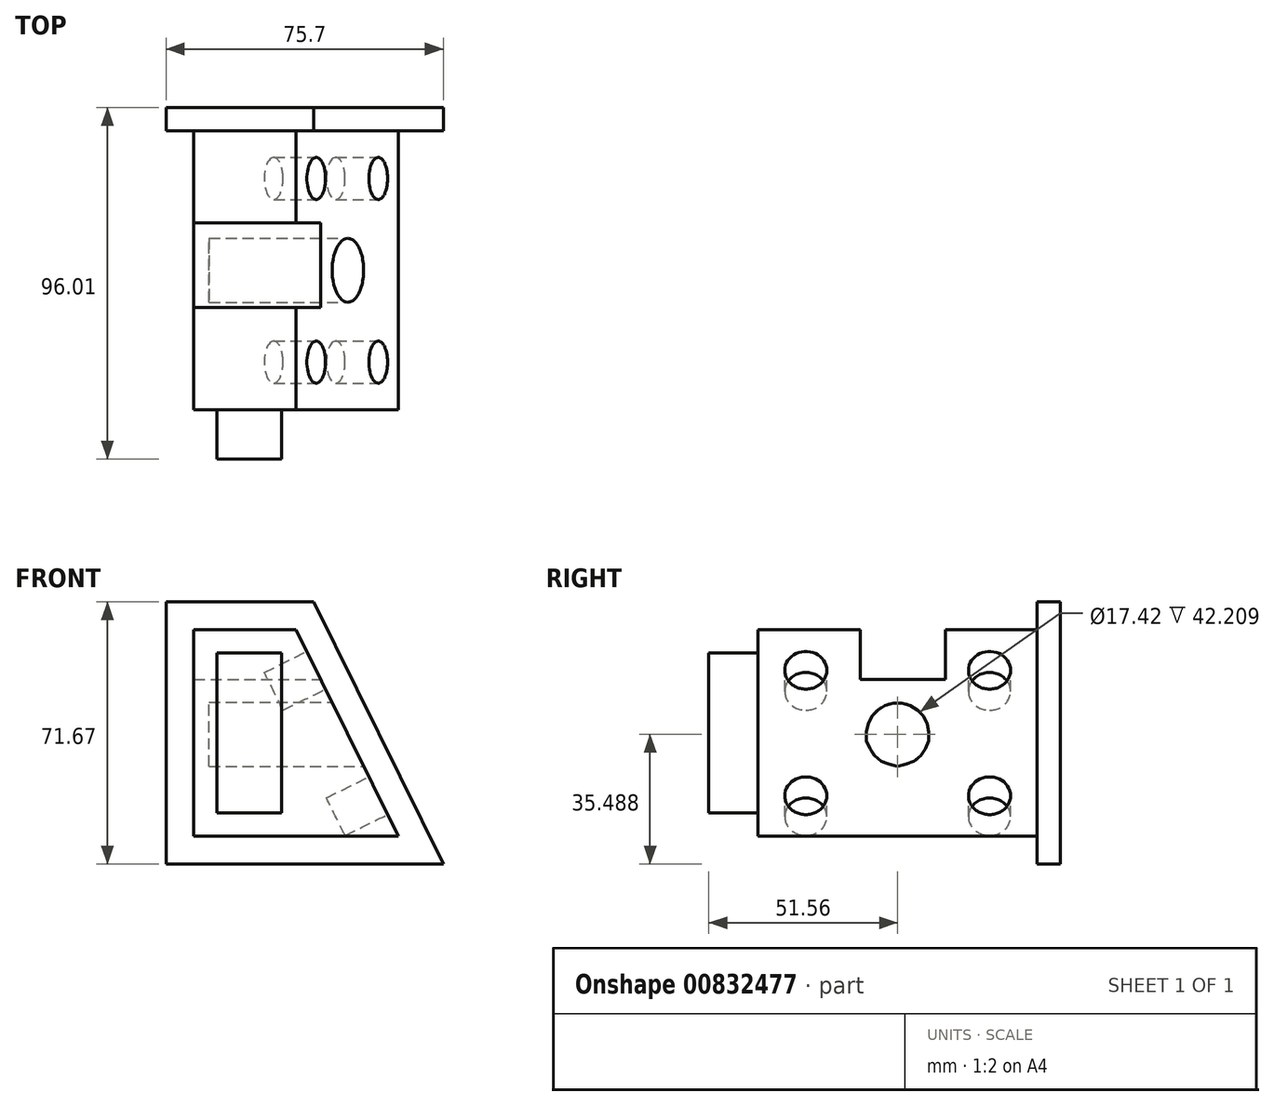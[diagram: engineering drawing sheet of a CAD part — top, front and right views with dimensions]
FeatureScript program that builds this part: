
annotation { "Feature Type Name" : "Feature", "Feature Type Description" : "" }
export const myFeature = defineFeature(function(context is Context, id is Id, definition is map)
    precondition{}
    {
        {
            var Q0;
            Q0=qCreatedBy(makeId("Front.planeOp"),FACE);
            var sketch = newSketch(context, id + "F0", { "sketchPlane" : qUnion([Q0])});
            skLineSegment(sketch, "E0.bottom", {"start": v(29.58, 0) * mm, "end": v(-26.23, 0) * mm});
            skLineSegment(sketch, "E0.right", {"start": v(-26.23, 0) * mm, "end": v(-26.23, 56.43) * mm});
            skLineSegment(sketch, "E1", {"start": v(-26.23, 56.43) * mm, "end": v(1.68, 56.43) * mm});
            skLineSegment(sketch, "E2", {"start": v(1.68, 56.43) * mm, "end": v(29.58, 0) * mm});
            skPoint(sketch, "E3.orphan", {"position": v(29.58, 56.43) * mm});
            skSolve(sketch);
        }
        {
            var Q0;
            Q0 = qSketchRegion(id + "F0", true);
            extrude(context, id + "F1", {"entities" : qUnion([Q0]), "endBound" : BoundingType.SYMMETRIC, "depth" : 76.2 * mm, "offsetDistance" : 25.4 * mm});
        }
        {
            var Q0;
            Q0=qCreatedBy(makeId("Right.planeOp"),FACE);
            var sketch = newSketch(context, id + "F2", { "sketchPlane" : qUnion([Q0])});
            skCircle(sketch, "E4", {"center": v(0, 27.87) * mm, "radius": 8.7 * mm});
            skSolve(sketch);
        }
        {
            var Q0;
            Q0 = qSketchRegion(id + "F2", true);
            extrude(context, id + "F3", {"entities" : qUnion([Q0]), "operationType" : NewBodyOperationType.REMOVE, "endBound" : BoundingType.SYMMETRIC, "oppositeDirection" : true, "depth" : 44.2 * mm, "offsetDistance" : 25.4 * mm});
        }
        {
            var Q0;
            Q0=makeQuery(id+"F1.opExtrude","CAP_FACE",FACE,{"disambiguationData":[OSD([sQuery(id+"F0.wireOp",EDGE,"E0.bottom"),sQuery(id+"F0.wireOp",EDGE,"E0.right"),sQuery(id+"F0.wireOp",EDGE,"E1"),sQuery(id+"F0.wireOp",EDGE,"E2")])],"isStart":true});
            var sketch = newSketch(context, id + "F4", { "sketchPlane" : qUnion([Q0])});
            skLineSegment(sketch, "E5.0", {"start": v(-6.41, 64.05) * mm, "end": v(-41.85, -7.62) * mm});
            skLineSegment(sketch, "E5.1", {"start": v(33.85, 64.05) * mm, "end": v(-6.41, 64.05) * mm});
            skLineSegment(sketch, "E5.2", {"start": v(33.85, -7.62) * mm, "end": v(33.85, 64.05) * mm});
            skLineSegment(sketch, "E5.3", {"start": v(-41.85, -7.62) * mm, "end": v(33.85, -7.62) * mm});
            skSolve(sketch);
        }
        {
            var Q0;
            Q0 = qSketchRegion(id + "F4", true);
            extrude(context, id + "F5", {"entities" : qUnion([Q0]), "operationType" : NewBodyOperationType.ADD, "depth" : 6.35 * mm, "offsetDistance" : 25.4 * mm});
        }
        {
            var Q0;
            Q0=makeQuery(id+"F1.opExtrude","SWEPT_FACE",FACE,{"disambiguationData":[OSD([sQuery(id+"F0.wireOp",EDGE,"E2")])]});
            var sketch = newSketch(context, id + "F6", { "sketchPlane" : qUnion([Q0])});
            skCircle(sketch, "E6", {"center": v(-25.08, 37.47) * mm, "radius": 5.74 * mm});
            skLineSegment(sketch, "E7", {"start": v(0, -13.11) * mm, "end": v(0, 49.84) * mm, "construction": true});
            skCircle(sketch, "E8.MirrorC", {"center": v(25.08, 37.47) * mm, "radius": 5.74 * mm});
            skLineSegment(sketch, "E9", {"start": v(-38.1, 18.36) * mm, "end": v(38.1, 18.36) * mm, "construction": true});
            skCircle(sketch, "E10.MirrorC", {"center": v(-25.08, -0.75) * mm, "radius": 5.74 * mm});
            skCircle(sketch, "E11.MirrorC", {"center": v(25.08, -0.75) * mm, "radius": 5.74 * mm});
            skSolve(sketch);
        }
        {
            var Q0;
            Q0 = qSketchRegion(id + "F6", true);
            extrude(context, id + "F7", {"entities" : qUnion([Q0]), "operationType" : NewBodyOperationType.REMOVE, "oppositeDirection" : true, "depth" : 12.95 * mm, "offsetDistance" : 25.4 * mm});
        }
        {
            var Q0;
            Q0=qCreatedBy(makeId("Right.planeOp"),FACE);
            var sketch = newSketch(context, id + "F8", { "sketchPlane" : qUnion([Q0])});
            skLineSegment(sketch, "E12.bottom", {"start": v(-10.16, 56.43) * mm, "end": v(12.98, 56.43) * mm});
            skLineSegment(sketch, "E12.top", {"start": v(-10.16, 42.83) * mm, "end": v(12.98, 42.83) * mm});
            skLineSegment(sketch, "E12.left", {"start": v(-10.16, 56.43) * mm, "end": v(-10.16, 42.83) * mm});
            skLineSegment(sketch, "E12.right", {"start": v(12.98, 56.43) * mm, "end": v(12.98, 42.83) * mm});
            skSolve(sketch);
        }
        {
            var Q0;
            Q0 = qSketchRegion(id + "F8", true);
            extrude(context, id + "F9", {"entities" : qUnion([Q0]), "operationType" : NewBodyOperationType.REMOVE, "endBound" : BoundingType.SYMMETRIC, "oppositeDirection" : true, "depth" : 56.9 * mm, "offsetDistance" : 25.4 * mm});
        }
        {
            var Q0;
            Q0=makeQuery(id+"F1.opExtrude","CAP_FACE",FACE,{"disambiguationData":[OSD([sQuery(id+"F0.wireOp",EDGE,"E0.bottom"),sQuery(id+"F0.wireOp",EDGE,"E0.right"),sQuery(id+"F0.wireOp",EDGE,"E1"),sQuery(id+"F0.wireOp",EDGE,"E2")])],"isStart":false});
            var sketch = newSketch(context, id + "F10", { "sketchPlane" : qUnion([Q0])});
            skLineSegment(sketch, "E13.1", {"start": v(-19.88, 6.35) * mm, "end": v(-2.27, 6.35) * mm});
            skLineSegment(sketch, "E13.2", {"start": v(-19.88, 50.08) * mm, "end": v(-19.88, 6.35) * mm});
            skLineSegment(sketch, "E13.3", {"start": v(-2.27, 50.08) * mm, "end": v(-19.88, 50.08) * mm});
            skLineSegment(sketch, "E14", {"start": v(-2.27, 50.08) * mm, "end": v(-2.27, 6.35) * mm});
            skPoint(sketch, "E14.endSnap0", {"position": v(-0.26, 6.35) * mm});
            skPoint(sketch, "E13.0.start.orphan", {"position": v(19.36, 6.35) * mm});
            skSolve(sketch);
        }
        {
            var Q0;
            Q0 = qSketchRegion(id + "F10", true);
            extrude(context, id + "F11", {"entities" : qUnion([Q0]), "operationType" : NewBodyOperationType.ADD, "depth" : 13.46 * mm, "offsetDistance" : 25.4 * mm});
        }
    });
